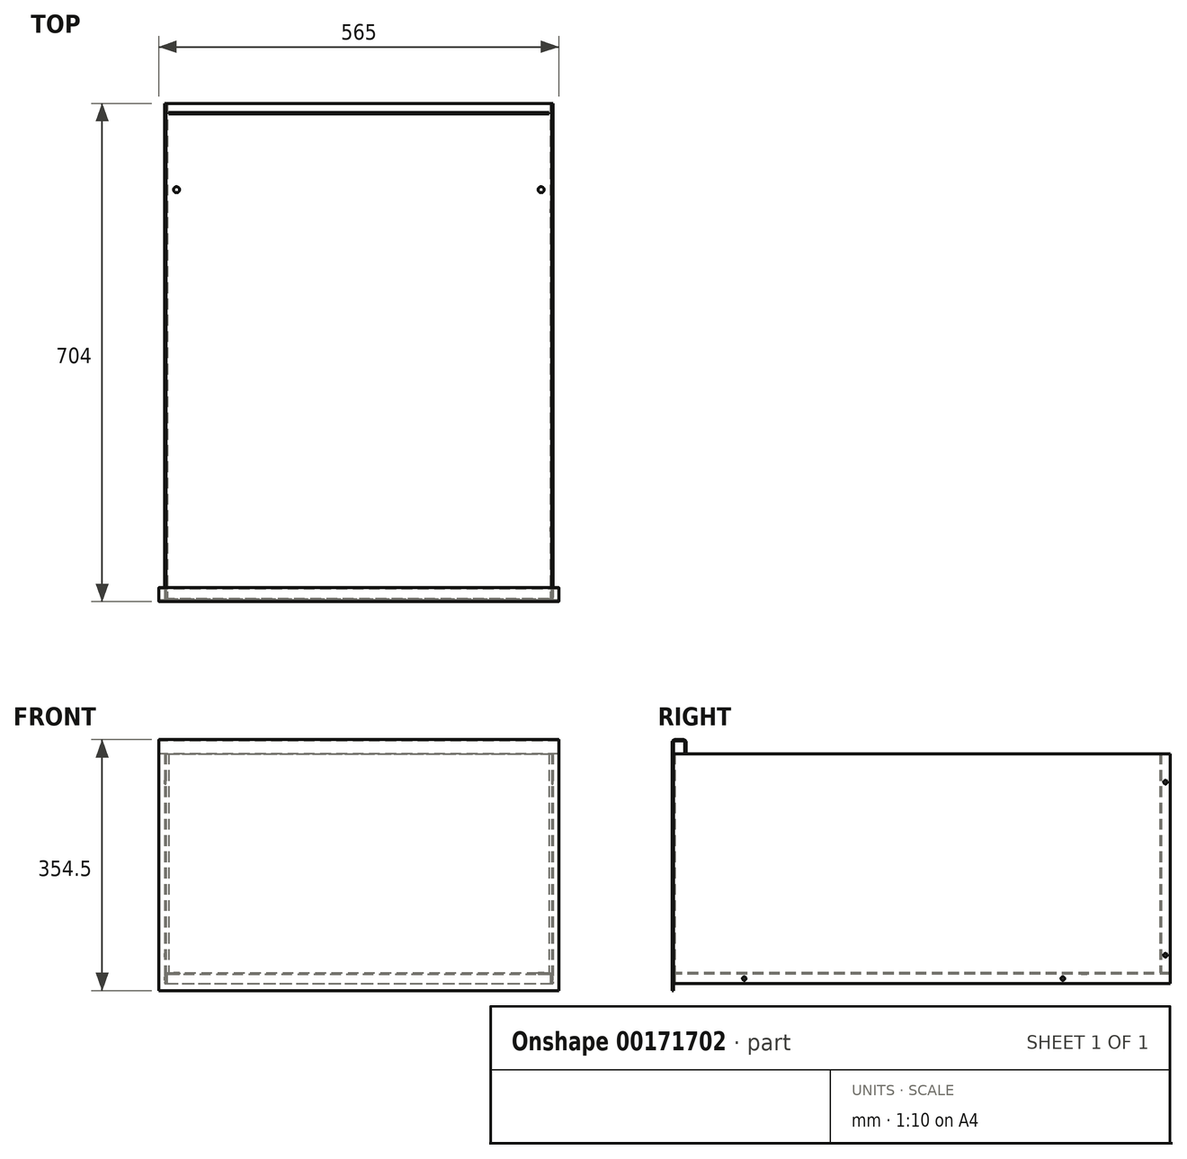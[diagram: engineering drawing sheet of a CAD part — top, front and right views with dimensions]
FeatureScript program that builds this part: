
annotation { "Feature Type Name" : "Feature", "Feature Type Description" : "" }
export const myFeature = defineFeature(function(context is Context, id is Id, definition is map)
    precondition{}
    {
        {
            var Q0;
            Q0=qCreatedBy(makeId("Top.planeOp"),FACE);
            var sketch = newSketch(context, id + "F0", { "sketchPlane" : qUnion([Q0])});
            skLineSegment(sketch, "E0.top", {"start": v(-270.5, -351) * mm, "end": v(270.5, -351) * mm});
            skLineSegment(sketch, "E0.left", {"start": v(-274.5, 351) * mm, "end": v(-274.5, -347) * mm});
            skLineSegment(sketch, "E0.right", {"start": v(274.5, 351) * mm, "end": v(274.5, -347) * mm});
            skPoint(sketch, "E0.middle", {"position": v(0, 0) * mm});
            skLineSegment(sketch, "E1", {"start": v(-274.5, 351) * mm, "end": v(274.5, 351) * mm, "construction": true});
            skLineSegment(sketch, "E2", {"start": v(-274.5, 351) * mm, "end": v(-272.5, 351) * mm});
            skLineSegment(sketch, "E3", {"start": v(-272.5, 351) * mm, "end": v(-272.5, -349) * mm});
            skLineSegment(sketch, "E4", {"start": v(-272.5, -349) * mm, "end": v(272.5, -349) * mm});
            skLineSegment(sketch, "E5", {"start": v(272.5, -349) * mm, "end": v(272.5, 351) * mm});
            skPoint(sketch, "E6.visualSharp", {"position": v(-274.5, -351) * mm});
            skArc(sketch, "E6.filletArc", {"start": v(-274.5, -347) * mm, "mid": v(-273.33, -349.83) * mm, "end": v(-270.5, -351) * mm});
            skPoint(sketch, "E7.visualSharp", {"position": v(274.5, -351) * mm});
            skArc(sketch, "E7.filletArc", {"start": v(270.5, -351) * mm, "mid": v(273.33, -349.83) * mm, "end": v(274.5, -347) * mm});
            skLineSegment(sketch, "E8", {"start": v(272.5, 351) * mm, "end": v(274.5, 351) * mm});
            skSolve(sketch);
        }
        {
            var Q0;
            Q0=makeQuery(id+"F0.imprint","IMPRINT",FACE,{"disambiguationData":[TD([[makeQuery(id+"F0.imprint","IMPRINT",EDGE,{"derivedFrom":sQuery(id+"F0.wireOp",EDGE,"E0.top")}),1.0]])]});
            extrude(context, id + "F1", {"entities" : qUnion([Q0]), "depth" : 324.5 * mm});
        }
        {
            var Q0;
            Q0=makeQuery(id+"F1.opExtrude","SWEPT_FACE",FACE,{"disambiguationData":[OSD([sQuery(id+"F0.wireOp",EDGE,"E4")])]});
            var sketch = newSketch(context, id + "F2", { "sketchPlane" : qUnion([Q0])});
            skLineSegment(sketch, "E9", {"start": v(-272.5, 0) * mm, "end": v(-272.5, 11) * mm});
            skLineSegment(sketch, "E10", {"start": v(-268.5, 15) * mm, "end": v(268.5, 15) * mm});
            skLineSegment(sketch, "E11", {"start": v(272.5, 11) * mm, "end": v(272.5, 0) * mm});
            skLineSegment(sketch, "E12", {"start": v(272.5, 0) * mm, "end": v(270.5, 0) * mm});
            skLineSegment(sketch, "E13", {"start": v(270.5, 0) * mm, "end": v(270.5, 13) * mm});
            skLineSegment(sketch, "E14", {"start": v(270.5, 13) * mm, "end": v(-270.5, 13) * mm});
            skLineSegment(sketch, "E15", {"start": v(-270.5, 13) * mm, "end": v(-270.5, 0) * mm});
            skLineSegment(sketch, "E16", {"start": v(-270.5, 0) * mm, "end": v(-272.5, 0) * mm});
            skPoint(sketch, "E17.visualSharp", {"position": v(272.5, 15) * mm});
            skArc(sketch, "E17.filletArc", {"start": v(272.5, 11) * mm, "mid": v(271.33, 13.83) * mm, "end": v(268.5, 15) * mm});
            skPoint(sketch, "E18.visualSharp", {"position": v(-272.5, 15) * mm});
            skArc(sketch, "E18.filletArc", {"start": v(-268.5, 15) * mm, "mid": v(-271.33, 13.83) * mm, "end": v(-272.5, 11) * mm});
            skSolve(sketch);
        }
        {
            var Q0;
            Q0=makeQuery(id+"F2.imprint","IMPRINT",FACE,{"disambiguationData":[TD([[makeQuery(id+"F2.imprint","IMPRINT",EDGE,{"derivedFrom":sQuery(id+"F2.wireOp",EDGE,"E9")}),1.0]])]});
            var Q1;
            Q1=makeQuery(id+"F1.opExtrude","SWEPT_FACE",FACE,{"disambiguationData":[OSD([sQuery(id+"F0.wireOp",EDGE,"E2")])]});
            extrude(context, id + "F3", {"entities" : qUnion([Q0]), "endBound" : BoundingType.UP_TO_SURFACE, "endBoundEntityFace" : qUnion([Q1]), "depth" : 25 * mm});
        }
        {
            var Q0;
            Q0=makeQuery(id+"F3.opExtrude","SWEPT_FACE",FACE,{"disambiguationData":[OSD([sQuery(id+"F2.wireOp",EDGE,"E10")])]});
            var sketch = newSketch(context, id + "F4", { "sketchPlane" : qUnion([Q0])});
            skLineSegment(sketch, "E19.0", {"start": v(272.5, -349) * mm, "end": v(272.5, 351) * mm});
            skLineSegment(sketch, "E20.0", {"start": v(-272.5, 351) * mm, "end": v(-272.5, -349) * mm});
            skLineSegment(sketch, "E21", {"start": v(-272.5, 351) * mm, "end": v(-272.5, 340) * mm});
            skLineSegment(sketch, "E22", {"start": v(-268.5, 336) * mm, "end": v(268.5, 336) * mm});
            skLineSegment(sketch, "E23", {"start": v(272.5, 340) * mm, "end": v(272.5, 351) * mm});
            skLineSegment(sketch, "E24", {"start": v(272.5, 351) * mm, "end": v(270.5, 351) * mm});
            skLineSegment(sketch, "E25", {"start": v(270.5, 351) * mm, "end": v(270.5, 338) * mm});
            skLineSegment(sketch, "E26", {"start": v(270.5, 338) * mm, "end": v(-270.5, 338) * mm});
            skLineSegment(sketch, "E27", {"start": v(-270.5, 338) * mm, "end": v(-270.5, 351) * mm});
            skLineSegment(sketch, "E28", {"start": v(-270.5, 351) * mm, "end": v(-272.5, 351) * mm});
            skPoint(sketch, "E29.visualSharp", {"position": v(272.5, 336) * mm});
            skArc(sketch, "E29.filletArc", {"start": v(268.5, 336) * mm, "mid": v(271.33, 337.17) * mm, "end": v(272.5, 340) * mm});
            skPoint(sketch, "E30.visualSharp", {"position": v(-272.5, 336) * mm});
            skArc(sketch, "E30.filletArc", {"start": v(-272.5, 340) * mm, "mid": v(-271.33, 337.17) * mm, "end": v(-268.5, 336) * mm});
            skSolve(sketch);
        }
        {
            var Q0;
            {var subQ0=sQuery(id+"F4.wireOp",EDGE,"E22");Q0=makeQuery(id+"F4.imprint","IMPRINT",FACE,{"disambiguationData":[TD([[makeQuery(id+"F4.imprint","IMPRINT",EDGE,{"derivedFrom":subQ0}),1.0]])]});}
            var Q1;
            Q1=makeQuery(id+"F4.imprint","IMPRINT",FACE,{"disambiguationData":[TD([[makeQuery(id+"F4.imprint","IMPRINT",EDGE,{"derivedFrom":sQuery(id+"F4.wireOp",EDGE,"E21")}),1.0]])]});
            var Q2;
            Q2=makeQuery(id+"F4.imprint","IMPRINT",FACE,{"disambiguationData":[TD([[makeQuery(id+"F4.imprint","IMPRINT",EDGE,{"derivedFrom":sQuery(id+"F4.wireOp",EDGE,"E23")}),1.0]])]});
            var Q3;
            Q3=makeQuery(id+"F1.opExtrude","CAP_FACE",FACE,{"disambiguationData":[OSD([sQuery(id+"F0.wireOp",EDGE,"E0.top"),sQuery(id+"F0.wireOp",EDGE,"E0.left"),sQuery(id+"F0.wireOp",EDGE,"E0.right"),sQuery(id+"F0.wireOp",EDGE,"E2"),sQuery(id+"F0.wireOp",EDGE,"E3"),sQuery(id+"F0.wireOp",EDGE,"E4"),sQuery(id+"F0.wireOp",EDGE,"E5"),sQuery(id+"F0.wireOp",EDGE,"E6.filletArc"),sQuery(id+"F0.wireOp",EDGE,"E7.filletArc"),sQuery(id+"F0.wireOp",EDGE,"E8")])],"isStart":false});
            extrude(context, id + "F5", {"entities" : qUnion([Q0, Q1, Q2]), "endBound" : BoundingType.UP_TO_SURFACE, "endBoundEntityFace" : qUnion([Q3]), "depth" : 25 * mm});
        }
        {
            var Q0;
            Q0=makeQuery(id+"F1.opExtrude","SWEPT_FACE",FACE,{"disambiguationData":[OSD([sQuery(id+"F0.wireOp",EDGE,"E0.right")])]});
            var sketch = newSketch(context, id + "F6", { "sketchPlane" : qUnion([Q0])});
            skLineSegment(sketch, "E31.0", {"start": v(-351, 324.5) * mm, "end": v(-351, 0) * mm});
            skLineSegment(sketch, "E32", {"start": v(-374.1, 7) * mm, "end": v(407.57, 7) * mm, "construction": true});
            skLineSegment(sketch, "E33", {"start": v(344, -59.87) * mm, "end": v(344, 378.9) * mm, "construction": true});
            skPoint(sketch, "E34", {"position": v(-251, 7) * mm});
            skPoint(sketch, "E35", {"position": v(199, 7) * mm});
            skPoint(sketch, "E36", {"position": v(344, 284.5) * mm});
            skPoint(sketch, "E37", {"position": v(344, 40) * mm});
            skSolve(sketch);
        }
        {
            var Q0;
            Q0=sQuery(id+"F6.wireOp",VERTEX,"E37");
            var Q1;
            Q1=sQuery(id+"F6.wireOp",VERTEX,"E35");
            var Q2;
            Q2=sQuery(id+"F6.wireOp",VERTEX,"E36");
            var Q3;
            Q3=sQuery(id+"F6.wireOp",VERTEX,"E34");
            var Q4;
            Q4=makeQuery(id+"F1.opExtrude","SWEPT_BODY",BODY,{"disambiguationData":[OSD([sQuery(id+"F0.wireOp",EDGE,"E0.top"),sQuery(id+"F0.wireOp",EDGE,"E0.left"),sQuery(id+"F0.wireOp",EDGE,"E0.right"),sQuery(id+"F0.wireOp",EDGE,"E2"),sQuery(id+"F0.wireOp",EDGE,"E3"),sQuery(id+"F0.wireOp",EDGE,"E4"),sQuery(id+"F0.wireOp",EDGE,"E5"),sQuery(id+"F0.wireOp",EDGE,"E6.filletArc"),sQuery(id+"F0.wireOp",EDGE,"E7.filletArc"),sQuery(id+"F0.wireOp",EDGE,"E8")])]});
            var Q5;
            Q5=makeQuery(id+"F3.opExtrude","SWEPT_BODY",BODY,{"disambiguationData":[OSD([sQuery(id+"F2.wireOp",EDGE,"E9"),sQuery(id+"F2.wireOp",EDGE,"E10"),sQuery(id+"F2.wireOp",EDGE,"E11"),sQuery(id+"F2.wireOp",EDGE,"E12"),sQuery(id+"F2.wireOp",EDGE,"E13"),sQuery(id+"F2.wireOp",EDGE,"E14"),sQuery(id+"F2.wireOp",EDGE,"E15"),sQuery(id+"F2.wireOp",EDGE,"E16"),sQuery(id+"F2.wireOp",EDGE,"E17.filletArc"),sQuery(id+"F2.wireOp",EDGE,"E18.filletArc")])]});
            var Q6;
            Q6=makeQuery(id+"F5.opExtrude","SWEPT_BODY",BODY,{"disambiguationData":[OSD([sQuery(id+"F4.wireOp",EDGE,"E21"),sQuery(id+"F4.wireOp",EDGE,"E22"),sQuery(id+"F4.wireOp",EDGE,"E23"),sQuery(id+"F4.wireOp",EDGE,"E24"),sQuery(id+"F4.wireOp",EDGE,"E25"),sQuery(id+"F4.wireOp",EDGE,"E26"),sQuery(id+"F4.wireOp",EDGE,"E27"),sQuery(id+"F4.wireOp",EDGE,"E28"),sQuery(id+"F4.wireOp",EDGE,"E29.filletArc"),sQuery(id+"F4.wireOp",EDGE,"E30.filletArc")])]});
            hole(context, id + "F7", {"style" : HoleStyle.C_SINK, "endStyle" : HoleEndStyle.BLIND, "holeDiameter" : 5 * mm, "cSinkDiameter" : 5 * mm, "cSinkAngle" : 90 * degree, "holeDepth" : 2000 * mm, "startFromSketch" : true, "locations" : qUnion([Q0, Q1, Q2, Q3]), "scope" : qUnion([Q4, Q5, Q6])});
        }
        {
            var Q0;
            Q0=qCreatedBy(makeId("Right.planeOp"),FACE);
            var sketch = newSketch(context, id + "F8", { "sketchPlane" : qUnion([Q0])});
            skPoint(sketch, "E38.0", {"position": v(-351, 324.5) * mm});
            skPoint(sketch, "E39.0", {"position": v(-351, 0) * mm});
            skLineSegment(sketch, "E40.0", {"start": v(351, 324.5) * mm, "end": v(-347, 324.5) * mm});
            skLineSegment(sketch, "E41", {"start": v(-351, 324.5) * mm, "end": v(-351, 342.5) * mm});
            skLineSegment(sketch, "E42", {"start": v(-351, 342.5) * mm, "end": v(-335, 342.5) * mm});
            skLineSegment(sketch, "E43", {"start": v(-335, 342.5) * mm, "end": v(-335, 324.5) * mm});
            skLineSegment(sketch, "E44", {"start": v(-335, 324.5) * mm, "end": v(-333, 324.5) * mm});
            skLineSegment(sketch, "E45", {"start": v(-333, 324.5) * mm, "end": v(-333, 340.5) * mm});
            skLineSegment(sketch, "E46", {"start": v(-337, 344.5) * mm, "end": v(-349, 344.5) * mm});
            skLineSegment(sketch, "E47", {"start": v(-353, 340.5) * mm, "end": v(-353, 324.5) * mm});
            skLineSegment(sketch, "E48", {"start": v(-353, 324.5) * mm, "end": v(-351, 324.5) * mm});
            skPoint(sketch, "E49.visualSharp", {"position": v(-353, 344.5) * mm});
            skArc(sketch, "E49.filletArc", {"start": v(-349, 344.5) * mm, "mid": v(-351.83, 343.33) * mm, "end": v(-353, 340.5) * mm});
            skPoint(sketch, "E50.visualSharp", {"position": v(-333, 344.5) * mm});
            skArc(sketch, "E50.filletArc", {"start": v(-333, 340.5) * mm, "mid": v(-334.17, 343.33) * mm, "end": v(-337, 344.5) * mm});
            skLineSegment(sketch, "E51", {"start": v(-351, 0) * mm, "end": v(-351, -10) * mm});
            skLineSegment(sketch, "E52", {"start": v(-351, -10) * mm, "end": v(-353, -10) * mm});
            skLineSegment(sketch, "E53", {"start": v(-353, -10) * mm, "end": v(-353, 0) * mm});
            skLineSegment(sketch, "E54", {"start": v(-353, 0) * mm, "end": v(-351, 0) * mm});
            skLineSegment(sketch, "E55", {"start": v(-351, 0) * mm, "end": v(-351, 324.5) * mm});
            skLineSegment(sketch, "E56", {"start": v(-353, 324.5) * mm, "end": v(-353, 0) * mm});
            skSolve(sketch);
        }
        {
            var Q0;
            Q0=makeQuery(id+"F8.imprint","IMPRINT",FACE,{"disambiguationData":[TD([[makeQuery(id+"F8.imprint","IMPRINT",EDGE,{"derivedFrom":sQuery(id+"F8.wireOp",EDGE,"E51")}),-1.0]])]});
            var Q1;
            Q1=makeQuery(id+"F8.imprint","IMPRINT",FACE,{"disambiguationData":[TD([[makeQuery(id+"F8.imprint","IMPRINT",EDGE,{"derivedFrom":sQuery(id+"F8.wireOp",EDGE,"E48")}),-1.0]])]});
            var Q2;
            Q2=makeQuery(id+"F8.imprint","IMPRINT",FACE,{"disambiguationData":[TD([[makeQuery(id+"F8.imprint","IMPRINT",EDGE,{"derivedFrom":sQuery(id+"F8.wireOp",EDGE,"E41")}),1.0]])]});
            extrude(context, id + "F9", {"entities" : qUnion([Q0, Q1, Q2]), "endBound" : BoundingType.SYMMETRIC, "depth" : 565 * mm});
        }
        {
            var Q0;
            Q0=makeQuery(id+"F3.opExtrude","SWEPT_FACE",FACE,{"disambiguationData":[OSD([sQuery(id+"F2.wireOp",EDGE,"E14")])]});
            var sketch = newSketch(context, id + "F10", { "sketchPlane" : qUnion([Q0])});
            skLineSegment(sketch, "E57.0", {"start": v(-270.5, 248.5) * mm, "end": v(-270.5, 253.5) * mm});
            skLineSegment(sketch, "E58.0", {"start": v(-270.5, 349) * mm, "end": v(270.5, 349) * mm});
            skPoint(sketch, "E59", {"position": v(-270.5, 251) * mm});
            skLineSegment(sketch, "E60", {"start": v(449.8, -229) * mm, "end": v(-536.27, -229) * mm, "construction": true});
            skPoint(sketch, "E61", {"position": v(257.5, -229) * mm});
            skLineSegment(sketch, "E62.0", {"start": v(272.5, 349) * mm, "end": v(272.5, -351) * mm});
            skLineSegment(sketch, "E63.0", {"start": v(-272.5, -351) * mm, "end": v(-272.5, 349) * mm});
            skPoint(sketch, "E64", {"position": v(-257.5, -229) * mm});
            skSolve(sketch);
        }
        {
            var Q0;
            Q0=sQuery(id+"F10.wireOp",VERTEX,"E64");
            var Q1;
            Q1=sQuery(id+"F10.wireOp",VERTEX,"E61");
            var Q2;
            Q2=makeQuery(id+"F3.opExtrude","SWEPT_BODY",BODY,{"disambiguationData":[OSD([sQuery(id+"F2.wireOp",EDGE,"E9"),sQuery(id+"F2.wireOp",EDGE,"E10"),sQuery(id+"F2.wireOp",EDGE,"E11"),sQuery(id+"F2.wireOp",EDGE,"E12"),sQuery(id+"F2.wireOp",EDGE,"E13"),sQuery(id+"F2.wireOp",EDGE,"E14"),sQuery(id+"F2.wireOp",EDGE,"E15"),sQuery(id+"F2.wireOp",EDGE,"E16"),sQuery(id+"F2.wireOp",EDGE,"E17.filletArc"),sQuery(id+"F2.wireOp",EDGE,"E18.filletArc")])]});
            hole(context, id + "F11", {"style" : HoleStyle.C_SINK, "endStyle" : HoleEndStyle.BLIND, "holeDiameter" : 8.5 * mm, "cSinkDiameter" : 8.5 * mm, "cSinkAngle" : 90 * degree, "holeDepth" : 20 * mm, "startFromSketch" : true, "locations" : qUnion([Q0, Q1]), "scope" : qUnion([Q2])});
        }
    });
